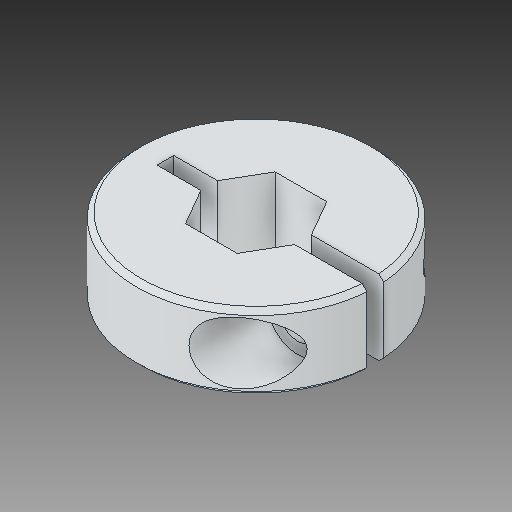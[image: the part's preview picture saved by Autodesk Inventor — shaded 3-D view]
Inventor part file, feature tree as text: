
AUTODESK INVENTOR PART (.ipt)
format: ipt  version: 2018 (Build 220112000, 112)  size: 140,288 bytes
history: native  units: in
note: dims shown in document units (in); Inventor stores cm internally (conversion verified against a paired STEP export)
features: chamfer x1
ambient origin geometry x8: Origin, YZ Plane, XZ Plane, XY Plane, X Axis, Y Axis, Z Axis, Center Point
bodies: Solid1 (feature_tree)
feature tree (1):
  chamfer  "Chamfer1"  [1 undecoded]
note: 1 required parameter value undecoded (feature->parameter linkage not recoverable at this tier; creation-order binding heuristic only, values carry confidence <= 0.55)
